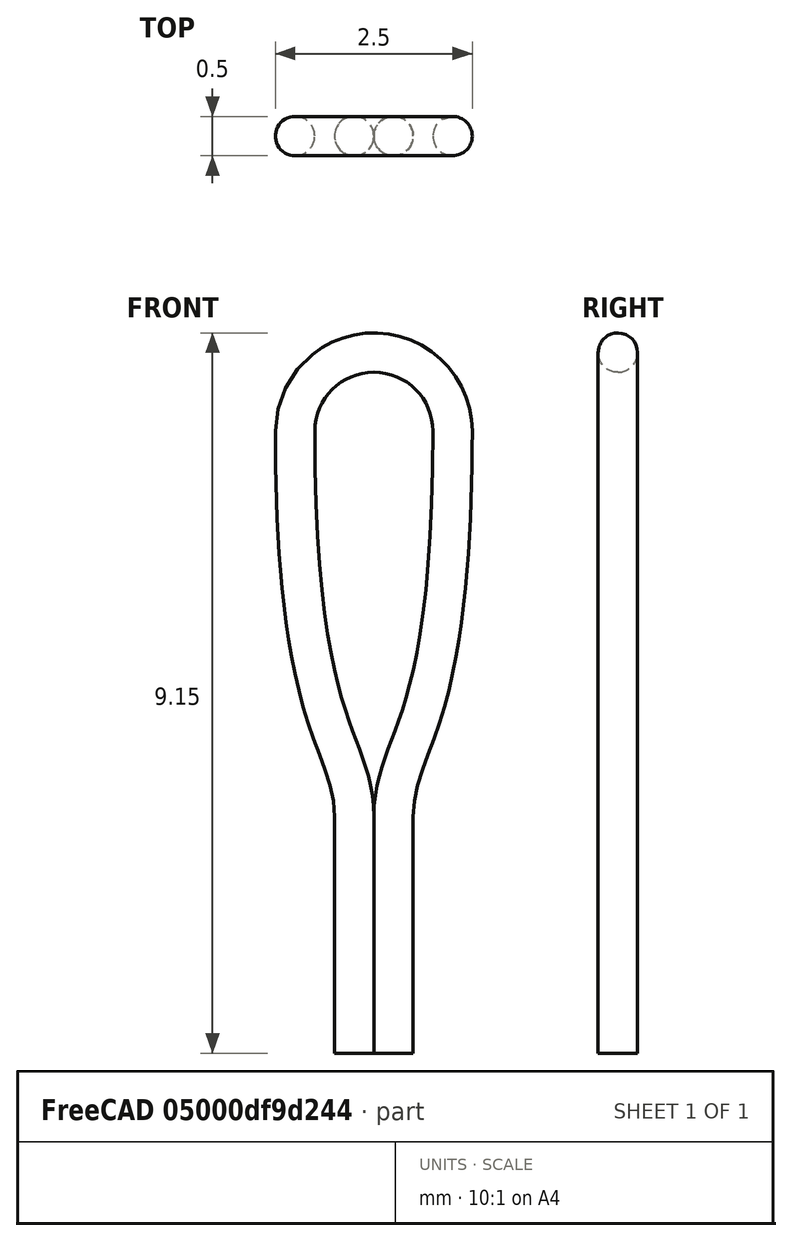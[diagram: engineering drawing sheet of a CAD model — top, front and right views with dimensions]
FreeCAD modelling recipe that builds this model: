
FCSTD DOCUMENT  (FreeCAD 0.17R12018 (Git))
Label: Test_Point_Loop_D2.50mm_Drill1.0mm
License: All rights reserved
LicenseURL: http://en.wikipedia.org/wiki/All_rights_reserved
objects: Sketcher::SketchObject×2, Spreadsheet::Sheet×1, PartDesign::AdditivePipe×1, PartDesign::Body×1, App::Part×1
note: 5 computed .brp shape members not serialized (recipe doc carries the construction recipe); baked Part::Feature solids carry a one-line shape summary decoded from their .brp

FEATURE [Spreadsheet::Sheet] Spreadsheet  label="dims"
  cells = A1="DWire"; B1(DWire)=0.5; A2="DLoop"; B2(DLoop)=2.5; A3="Spacer"; B3(Spacer)=0; A4="DSpacer"; B4(DSpacer)=3; A5="Lall"; B5(Lall)=8.9000000000000004; A6="Ddrill"; B6(Ddrill)=1; A7="Lbottom"; B7(Lbottom)=3
FEATURE [Sketcher::SketchObject] Sketch001
  MapMode = 5
  Placement = pos=(0,0,0) rot=(1,0,0;1.5708rad)
  expr: Constraints[63] = (dims.DLoop - dims.DWire) / 2
  expr: Constraints[28] = dims.Lall - (dims.DLoop - dims.DWire) / 2
  expr: Constraints[27] = (dims.DLoop - dims.DWire) / 2
  expr: Constraints[30] = dims.Lbottom
  expr: Constraints[32] = dims.Spacer
  expr: Constraints[33] = dims.Ddrill - dims.DWire
  expr: Constraints[34] = (dims.Ddrill - dims.DWire) / 2
  sketch-geometry (25):
    g0: LineSegment StartX=-0.25 StartY=-3 StartZ=0 EndX=-0.25 EndY=6.14334e-07 EndZ=0
    g1: LineSegment StartX=0.25 StartY=1.27817e-06 StartZ=0 EndX=0.25 EndY=-3 EndZ=0
    g2: ArcOfCircle CenterX=0 CenterY=4.9 CenterZ=0 NormalX=0 NormalY=0 NormalZ=1 Radius=1 StartAngle=0 EndAngle=3.14159
    g3: LineSegment [constr] StartX=-1 StartY=4.9 StartZ=0 EndX=1 EndY=4.9 EndZ=0
    g4: LineSegment [constr] StartX=-1 StartY=1.18228e-06 StartZ=0 EndX=1 EndY=1.18228e-06 EndZ=0
    g5: LineSegment [constr] StartX=1 StartY=4.9 StartZ=0 EndX=1 EndY=1.18228e-06 EndZ=0
    g6: LineSegment [constr] StartX=-1 StartY=1.18228e-06 StartZ=0 EndX=-1 EndY=4.9 EndZ=0
    g7: LineSegment [constr] StartX=-0.25 StartY=6.14334e-07 StartZ=0 EndX=-0.25 EndY=1 EndZ=0
    g8: LineSegment [constr] StartX=0.25 StartY=1.27817e-06 StartZ=0 EndX=0.25 EndY=1 EndZ=0
    g9: LineSegment [constr] StartX=-1 StartY=1 StartZ=0 EndX=1 EndY=1 EndZ=0
    g10: LineSegment [constr] StartX=0.25 StartY=1 StartZ=0 EndX=0.25 EndY=4.9 EndZ=0
    g11-g14: Circle [constr] x4 (B-spline internal-alignment scaffolding for g15; pole/knot coordinates omitted)
    g15: BSplineCurve PolesCount=4 KnotsCount=2 Degree=3 IsPeriodic=0
    g16: GeomPoint [constr] X=-0.25 Y=6.14334e-07 Z=0
    g17: GeomPoint [constr] X=-1 Y=4.9 Z=0
    g18-g21: Circle [constr] x4 (B-spline internal-alignment scaffolding for g22; pole/knot coordinates omitted)
    g22: BSplineCurve PolesCount=4 KnotsCount=2 Degree=3 IsPeriodic=0
    g23: GeomPoint [constr] X=0.25 Y=1.27817e-06 Z=0
    g24: GeomPoint [constr] X=1 Y=4.9 Z=0
  constraints (58):
    c: Vertical(g0)
    c: Vertical(g1)
    c: Coincident(g3,g2)
    c: Horizontal(g3)
    c: PointOnObject(g2,g3)
    c: Coincident(g3,g2)
    c: PointOnObject(g2,g-2)
    c: Horizontal(g4)
    c: Coincident(g5,g2)
    c: Coincident(g5,g4)
    c: Coincident(g6,g4)
    c: Coincident(g6,g2)
    c: PointOnObject(g0,g4)
    c: PointOnObject(g1,g4)
    c: Vertical(g6)
    c: Vertical(g5)
    c: Coincident(g7,g0)
    c: Vertical(g7)
    c: Coincident(g8,g1)
    c: Vertical(g8)
    c: PointOnObject(g9,g6)
    c: PointOnObject(g9,g5)
    c: Horizontal(g9)
    c: PointOnObject(g7,g9)
    c: PointOnObject(g8,g9)
    c: PointOnObject(g10,g3)
    c: Vertical(g10)
    c: Radius(g2) = 1
    c: DistanceY(g1,g2) = 7.9
    c: DistanceY(g1,g0) = 0
    c: DistanceY(g0,g-1) = 3
    c: Coincident(g10,g8)
    c: DistanceY(g-1,g0) = 0
    c: DistanceX(g0,g1) = 0.5
    c: DistanceX(g0,g-1) = 0.25
    c: Coincident(g11,g0)
    c: Radius(g11) = 0
    c: Equal(g11,g12)
    c: Coincident(g12,g7)
    c: Equal(g11,g13)
    c: Coincident(g13,g9)
    c: Equal(g11,g14)
    c: Coincident(g14,g2)
    c: InternalAlignment(g11-g14 -> g15) x4
    c: InternalAlignment(g16,g15)
    c: InternalAlignment(g17,g15)
    c: Coincident(g18,g1)
    c: Radius(g18) = 0
    c: Equal(g18,g19)
    c: Coincident(g19,g8)
    c: Equal(g18,g20)
    c: Coincident(g20,g9)
    c: Equal(g18,g21)
    c: Coincident(g21,g2)
    c: InternalAlignment(g18-g21 -> g22) x4
    c: InternalAlignment(g23,g22)
    c: InternalAlignment(g24,g22)
    c: DistanceY(g4,g9) = 1
FEATURE [Sketcher::SketchObject] Sketch
  MapMode = 5
  Placement = pos=(0,0,-3) rot=(0,0,1;0rad)
  expr: Constraints[2] = (dims.Ddrill - dims.DWire) / 2
  expr: Constraints[1] = dims.DWire / 2
  sketch-geometry (1):
    g0: Circle CenterX=-0.25 CenterY=0 CenterZ=0 NormalX=0 NormalY=0 NormalZ=1 Radius=0.25
  constraints (3):
    c: PointOnObject(g0,g-1)
    c: Radius(g0) = 0.25
    c: DistanceX(g0,g-1) = 0.25
FEATURE [PartDesign::AdditivePipe] AdditivePipe
  AuxilleryCurvelinear = true
  AuxillerySpineTangent = false
  Binormal = (0,0,0)
  Mode = 0
  Placement = pos=(0,0,-3) rot=(0,0,1;0rad)
  Profile = -> Sketch
  Spine = -> Sketch001 [Edge1,Edge2,Edge3,Edge4,Edge5]
  SpineTangent = false
  Transformation = 0
  Transition = 0
FEATURE [PartDesign::Body] Body  label="Test_Point_Loop_D2.50mm_Drill1.0mm"
  Group = -> [Sketch,Sketch001,AdditivePipe]
  Origin = -> Origin002
  Tip = -> AdditivePipe
FEATURE [App::Part] Part  label="group"
  Group = -> [Body]
  License = CC BY 3.0
  LicenseURL = http://creativecommons.org/licenses/by/3.0/
  Origin = -> Origin
